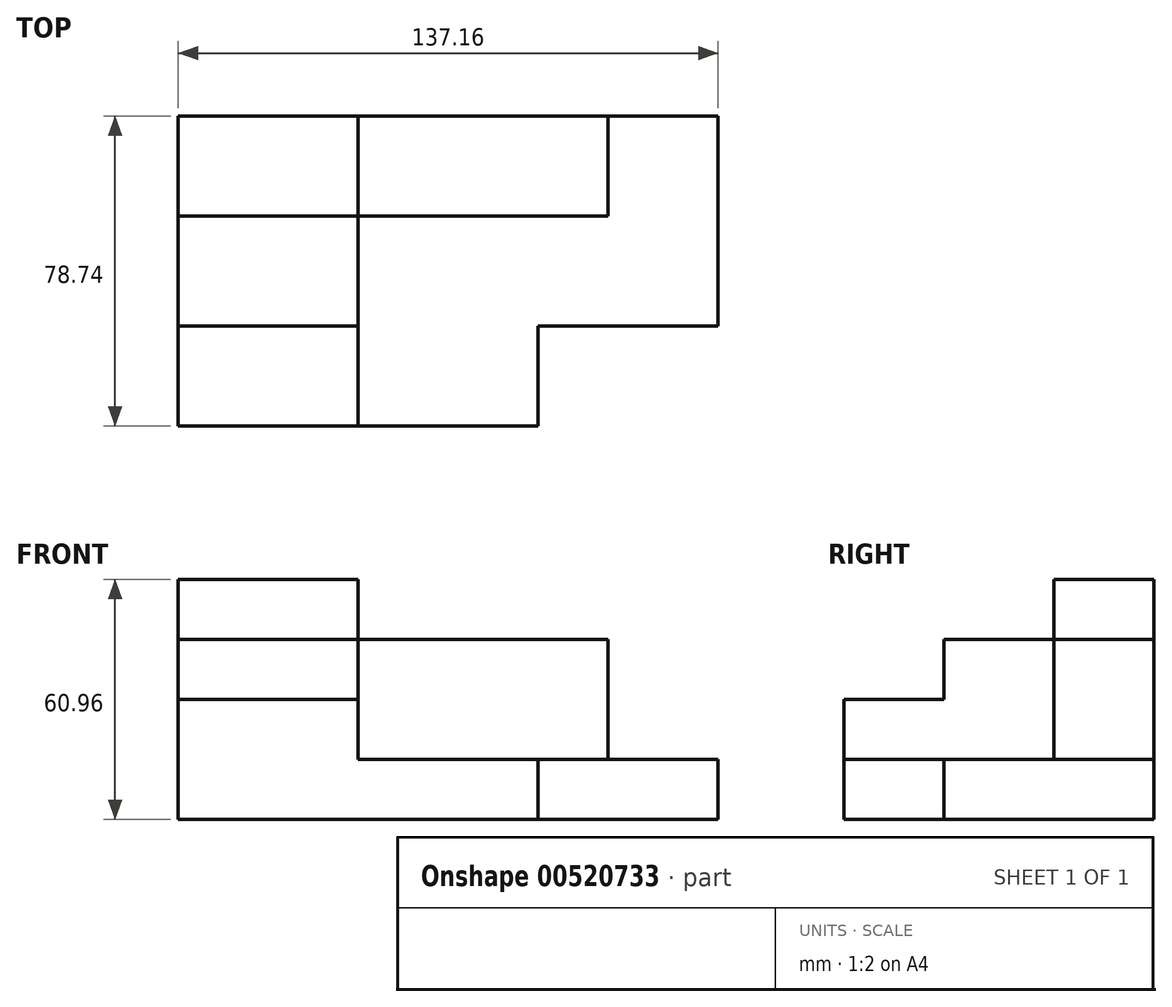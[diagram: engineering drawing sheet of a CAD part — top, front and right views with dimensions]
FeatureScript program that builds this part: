
annotation { "Feature Type Name" : "Feature", "Feature Type Description" : "" }
export const myFeature = defineFeature(function(context is Context, id is Id, definition is map)
    precondition{}
    {
        {
            var Q0;
            Q0=qCreatedBy(makeId("Front.planeOp"),FACE);
            var sketch = newSketch(context, id + "F0", { "sketchPlane" : qUnion([Q0])});
            skLineSegment(sketch, "E0.bottom", {"start": v(-23.16, 10.79) * mm, "end": v(114, 10.79) * mm});
            skLineSegment(sketch, "E0.top", {"start": v(-23.16, -50.17) * mm, "end": v(114, -50.17) * mm});
            skLineSegment(sketch, "E0.left", {"start": v(-23.16, 10.79) * mm, "end": v(-23.16, -50.17) * mm});
            skLineSegment(sketch, "E0.right", {"start": v(114, 10.79) * mm, "end": v(114, -50.17) * mm});
            skSolve(sketch);
        }
        {
            var Q0;
            Q0 = qSketchRegion(id + "F0", true);
            extrude(context, id + "F1", {"entities" : qUnion([Q0]), "depth" : 78.74 * mm, "offsetDistance" : 25.4 * mm});
        }
        {
            var Q0;
            Q0=makeQuery(id+"F1.opExtrude","SWEPT_FACE",FACE,{"disambiguationData":[OSD([sQuery(id+"F0.wireOp",EDGE,"E0.bottom")])]});
            var sketch = newSketch(context, id + "F2", { "sketchPlane" : qUnion([Q0])});
            skLineSegment(sketch, "E1.bottom", {"start": v(-23.16, 0) * mm, "end": v(22.56, 0) * mm});
            skLineSegment(sketch, "E1.top", {"start": v(-23.16, -25.4) * mm, "end": v(22.56, -25.4) * mm});
            skLineSegment(sketch, "E1.left", {"start": v(-23.16, 0) * mm, "end": v(-23.16, -25.4) * mm});
            skLineSegment(sketch, "E1.right", {"start": v(22.56, 0) * mm, "end": v(22.56, -25.4) * mm});
            skLineSegment(sketch, "E2.bottom", {"start": v(-23.16, -78.74) * mm, "end": v(22.56, -78.74) * mm});
            skLineSegment(sketch, "E2.top", {"start": v(-23.16, -53.34) * mm, "end": v(22.56, -53.34) * mm});
            skLineSegment(sketch, "E2.left", {"start": v(-23.16, -78.74) * mm, "end": v(-23.16, -53.34) * mm});
            skLineSegment(sketch, "E2.right", {"start": v(22.56, -78.74) * mm, "end": v(22.56, -53.34) * mm});
            skLineSegment(sketch, "E3", {"start": v(22.56, -25.4) * mm, "end": v(22.56, -53.34) * mm});
            skLineSegment(sketch, "E4.bottom", {"start": v(22.56, 0) * mm, "end": v(86.06, 0) * mm});
            skLineSegment(sketch, "E4.top", {"start": v(22.56, -25.4) * mm, "end": v(86.06, -25.4) * mm});
            skLineSegment(sketch, "E4.right", {"start": v(86.06, 0) * mm, "end": v(86.06, -25.4) * mm});
            skLineSegment(sketch, "E5.bottom", {"start": v(68.28, -53.34) * mm, "end": v(114, -53.34) * mm});
            skLineSegment(sketch, "E5.top", {"start": v(68.28, -78.74) * mm, "end": v(114, -78.74) * mm});
            skLineSegment(sketch, "E5.left", {"start": v(68.28, -53.34) * mm, "end": v(68.28, -78.74) * mm});
            skLineSegment(sketch, "E5.right", {"start": v(114, -53.34) * mm, "end": v(114, -78.74) * mm});
            skSolve(sketch);
        }
        {
            var Q0;
            Q0=makeQuery(id+"F2.imprint","IMPRINT",FACE,{"disambiguationData":[TD([[makeQuery(id+"F2.imprint","IMPRINT",EDGE,{"derivedFrom":sQuery(id+"F2.wireOp",EDGE,"E5.bottom")}),-1.0]])]});
            extrude(context, id + "F3", {"entities" : qUnion([Q0]), "operationType" : NewBodyOperationType.REMOVE, "endBound" : BoundingType.THROUGH_ALL, "oppositeDirection" : true, "depth" : 25.4 * mm, "offsetDistance" : 25.4 * mm});
        }
        {
            var Q0;
            {var subQ5=sQuery(id+"F2.wireOp",EDGE,"E2.right");Q0=makeQuery(id+"F2.imprint","IMPRINT",FACE,{"disambiguationData":[TD([[makeQuery(id+"F2.imprint","IMPRINT",EDGE,{"derivedFrom":subQ5}),-1.0]])]});}
            extrude(context, id + "F4", {"entities" : qUnion([Q0]), "operationType" : NewBodyOperationType.REMOVE, "oppositeDirection" : true, "depth" : 45.72 * mm, "offsetDistance" : 25.4 * mm});
        }
        {
            var Q0;
            Q0=makeQuery(id+"F2.imprint","IMPRINT",FACE,{"disambiguationData":[TD([[makeQuery(id+"F2.imprint","IMPRINT",EDGE,{"derivedFrom":sQuery(id+"F2.wireOp",EDGE,"E4.bottom")}),-1.0]])]});
            extrude(context, id + "F5", {"entities" : qUnion([Q0]), "operationType" : NewBodyOperationType.REMOVE, "oppositeDirection" : true, "depth" : 15.24 * mm, "offsetDistance" : 25.4 * mm});
        }
        {
            var Q0;
            {var subQ0=sQuery(id+"F2.wireOp",EDGE,"E1.top");Q0=makeQuery(id+"F2.imprint","IMPRINT",FACE,{"disambiguationData":[TD([[makeQuery(id+"F2.imprint","IMPRINT",EDGE,{"derivedFrom":subQ0}),-1.0]])]});}
            extrude(context, id + "F6", {"entities" : qUnion([Q0]), "operationType" : NewBodyOperationType.REMOVE, "oppositeDirection" : true, "depth" : 15.24 * mm, "offsetDistance" : 25.4 * mm});
        }
        {
            var Q0;
            Q0=makeQuery(id+"F2.imprint","IMPRINT",FACE,{"disambiguationData":[TD([[makeQuery(id+"F2.imprint","IMPRINT",EDGE,{"derivedFrom":sQuery(id+"F2.wireOp",EDGE,"E2.bottom")}),1.0]])]});
            extrude(context, id + "F7", {"entities" : qUnion([Q0]), "operationType" : NewBodyOperationType.REMOVE, "oppositeDirection" : true, "depth" : 30.48 * mm, "offsetDistance" : 25.4 * mm});
        }
    });
